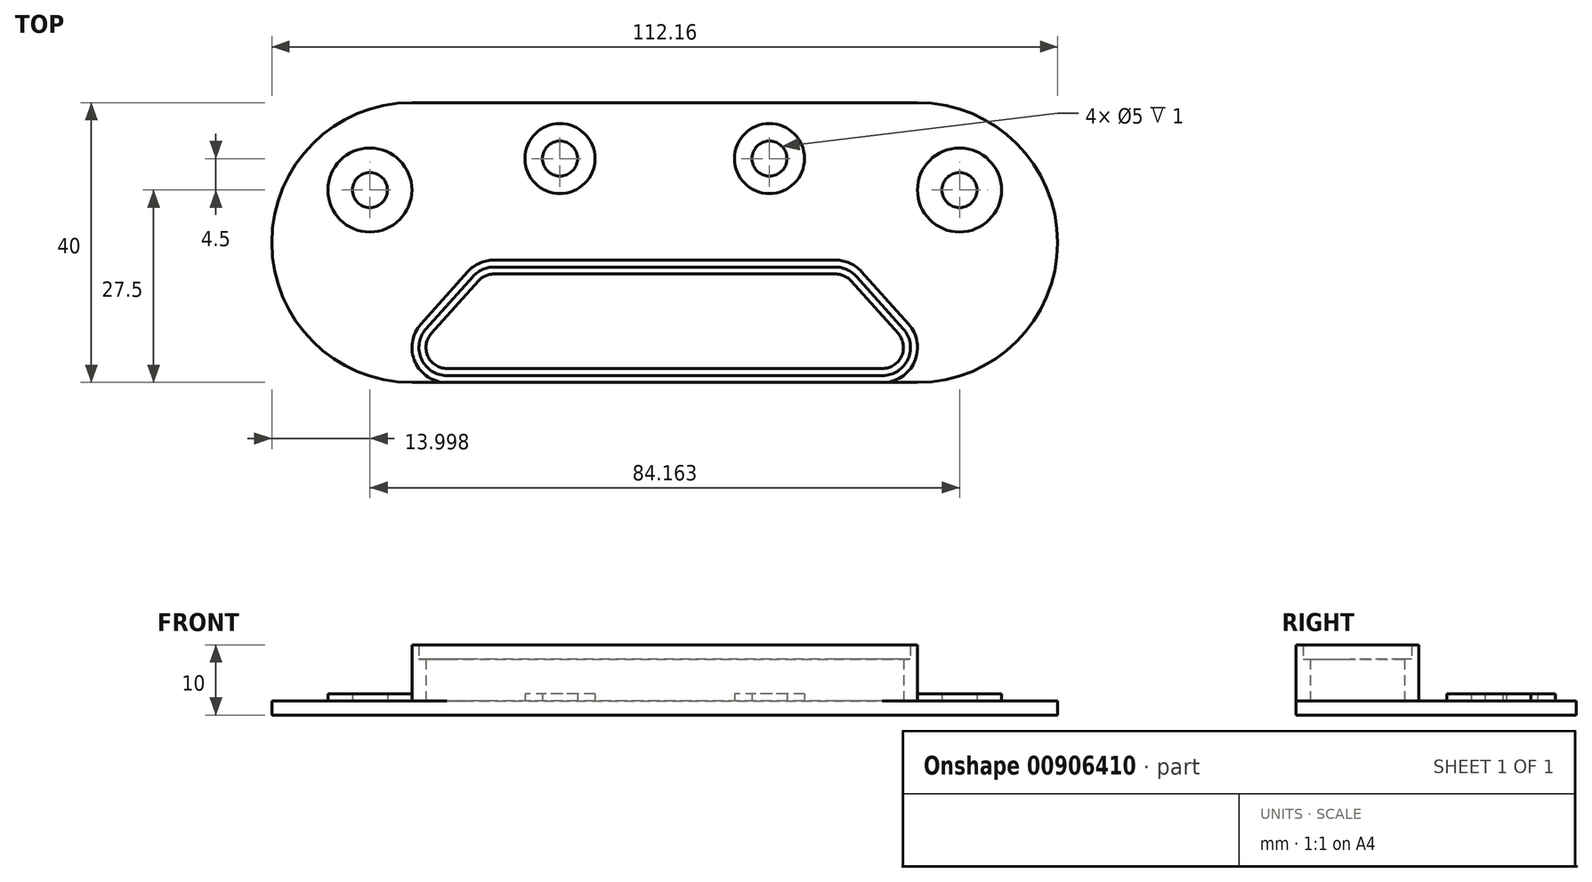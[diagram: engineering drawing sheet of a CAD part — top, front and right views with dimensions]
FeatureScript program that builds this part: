
annotation { "Feature Type Name" : "Feature", "Feature Type Description" : "" }
export const myFeature = defineFeature(function(context is Context, id is Id, definition is map)
    precondition{}
    {
        {
            var Q0;
            Q0=qCreatedBy(makeId("Top.planeOp"),FACE);
            var sketch = newSketch(context, id + "F0", { "sketchPlane" : qUnion([Q0])});
            skLineSegment(sketch, "E0.bottom", {"start": v(36.08, -20) * mm, "end": v(-36.08, -20) * mm});
            skLineSegment(sketch, "E0.top", {"start": v(36.08, 20) * mm, "end": v(-36.08, 20) * mm});
            skLineSegment(sketch, "E0.left", {"start": v(56.08, 0) * mm, "end": v(56.08, 0) * mm});
            skLineSegment(sketch, "E0.right", {"start": v(-56.08, 0) * mm, "end": v(-56.08, 0) * mm});
            skPoint(sketch, "E0.middle", {"position": v(0, 0) * mm});
            skPoint(sketch, "E1.visualSharp", {"position": v(-56.08, -20) * mm});
            skArc(sketch, "E1.filletArc", {"start": v(-56.08, 0) * mm, "mid": v(-50.22, -14.14) * mm, "end": v(-36.08, -20) * mm});
            skPoint(sketch, "E2.visualSharp", {"position": v(-56.08, 20) * mm});
            skArc(sketch, "E2.filletArc", {"start": v(-36.08, 20) * mm, "mid": v(-50.22, 14.14) * mm, "end": v(-56.08, 0) * mm});
            skPoint(sketch, "E3.visualSharp", {"position": v(56.08, 20) * mm});
            skArc(sketch, "E3.filletArc", {"start": v(56.08, 0) * mm, "mid": v(50.22, 14.14) * mm, "end": v(36.08, 20) * mm});
            skPoint(sketch, "E4.visualSharp", {"position": v(56.08, -20) * mm});
            skArc(sketch, "E4.filletArc", {"start": v(36.08, -20) * mm, "mid": v(50.22, -14.14) * mm, "end": v(56.08, 0) * mm});
            skSolve(sketch);
        }
        {
            var Q0;
            Q0=qSketchRegion(id+"F0",true);
            extrude(context, id + "F1", {"entities" : qUnion([Q0]), "depth" : 2 * mm, "offsetDistance" : 25 * mm});
        }
        {
            var Q0;
            Q0=makeQuery(id+"F1.opExtrude","CAP_FACE",FACE,{"disambiguationData":[OSD([sQuery(id+"F0.wireOp",EDGE,"E0.bottom"),sQuery(id+"F0.wireOp",EDGE,"E0.top"),sQuery(id+"F0.wireOp",EDGE,"E1.filletArc"),sQuery(id+"F0.wireOp",EDGE,"E2.filletArc"),sQuery(id+"F0.wireOp",EDGE,"E3.filletArc"),sQuery(id+"F0.wireOp",EDGE,"E4.filletArc")])],"isStart":false});
            var sketch = newSketch(context, id + "F2", { "sketchPlane" : qUnion([Q0])});
            skLineSegment(sketch, "E5", {"start": v(-76.8, 0) * mm, "end": v(76.55, 0) * mm, "construction": true});
            skLineSegment(sketch, "E6", {"start": v(0, -28.1) * mm, "end": v(0, 41.06) * mm, "construction": true});
            skPoint(sketch, "E6.endSnap0", {"position": v(0, 20) * mm});
            skCircle(sketch, "E7", {"center": v(-42.08, 7.5) * mm, "radius": 6 * mm});
            skCircle(sketch, "E8", {"center": v(-42.08, 7.5) * mm, "radius": 2.5 * mm});
            skCircle(sketch, "E9", {"center": v(-14.95, 12) * mm, "radius": 5 * mm});
            skCircle(sketch, "E10", {"center": v(-14.95, 12) * mm, "radius": 2.5 * mm});
            skCircle(sketch, "E11.MirrorC", {"center": v(42.08, 7.5) * mm, "radius": 2.5 * mm});
            skCircle(sketch, "E12.MirrorC", {"center": v(42.08, 7.5) * mm, "radius": 6 * mm});
            skCircle(sketch, "E13.MirrorC", {"center": v(14.95, 12) * mm, "radius": 5 * mm});
            skCircle(sketch, "E14.MirrorC", {"center": v(14.95, 12) * mm, "radius": 2.5 * mm});
            skSolve(sketch);
        }
        {
            var Q0;
            Q0=qSketchRegion(id+"F2",true);
            extrude(context, id + "F3", {"entities" : qUnion([Q0]), "operationType" : NewBodyOperationType.ADD, "depth" : 1 * mm, "offsetDistance" : 25 * mm});
        }
        {
            var Q0;
            {var subQ0=sQuery(id+"F0.wireOp",EDGE,"E2.filletArc");var subQ1=sQuery(id+"F0.wireOp",EDGE,"E1.filletArc");var subQ2=sQuery(id+"F0.wireOp",EDGE,"E0.top");var subQ3=sQuery(id+"F0.wireOp",EDGE,"E4.filletArc");var subQ4=sQuery(id+"F0.wireOp",EDGE,"E3.filletArc");var subQ5=sQuery(id+"F0.wireOp",EDGE,"E0.bottom");Q0=makeQuery(id+"F3.boolean.opBoolean","SPLIT",FACE,{"disambiguationData":[TD([makeQuery(id+"F1.opExtrude","SWEPT_FACE",FACE,{"disambiguationData":[OSD([subQ5])]})])],"derivedFrom":makeQuery(id+"F1.opExtrude","CAP_FACE",FACE,{"disambiguationData":[OSD([subQ5,subQ2,subQ1,subQ0,subQ4,subQ3])],"isStart":false})});}
            var sketch = newSketch(context, id + "F4", { "sketchPlane" : qUnion([Q0])});
            skLineSegment(sketch, "E15", {"start": v(0, 31.88) * mm, "end": v(0, -36.97) * mm, "construction": true});
            skLineSegment(sketch, "E16", {"start": v(0, -20) * mm, "end": v(-31.08, -20) * mm});
            skLineSegment(sketch, "E17", {"start": v(-34.8, -11.67) * mm, "end": v(-28.1, -4.17) * mm});
            skLineSegment(sketch, "E18", {"start": v(-24.38, -2.5) * mm, "end": v(0, -2.5) * mm});
            skPoint(sketch, "E19.visualSharp", {"position": v(-42.26, -20) * mm});
            skArc(sketch, "E19.filletArc", {"start": v(-34.8, -11.67) * mm, "mid": v(-35.65, -17.04) * mm, "end": v(-31.08, -20) * mm});
            skPoint(sketch, "E20.visualSharp", {"position": v(-26.61, -2.5) * mm});
            skArc(sketch, "E20.filletArc", {"start": v(-24.38, -2.5) * mm, "mid": v(-26.42, -2.94) * mm, "end": v(-28.1, -4.17) * mm});
            skLineSegment(sketch, "E21.0", {"start": v(0, -19) * mm, "end": v(-31.08, -19) * mm});
            skLineSegment(sketch, "E21.1", {"start": v(-24.38, -3.5) * mm, "end": v(0, -3.5) * mm});
            skArc(sketch, "E21.2", {"start": v(-24.38, -3.5) * mm, "mid": v(-26, -3.85) * mm, "end": v(-27.36, -4.83) * mm});
            skLineSegment(sketch, "E21.3", {"start": v(-34.06, -12.33) * mm, "end": v(-27.36, -4.83) * mm});
            skArc(sketch, "E21.4", {"start": v(-34.06, -12.33) * mm, "mid": v(-34.73, -16.63) * mm, "end": v(-31.08, -19) * mm});
            skPoint(sketch, "E22.MirrorP", {"position": v(26.61, -2.5) * mm});
            skLineSegment(sketch, "E23.MirrorCS", {"start": v(0, -19) * mm, "end": v(31.08, -19) * mm});
            skArc(sketch, "E24.MirrorCS", {"start": v(24.38, -2.5) * mm, "mid": v(26.42, -2.94) * mm, "end": v(28.1, -4.17) * mm});
            skArc(sketch, "E25.MirrorCS", {"start": v(34.06, -12.33) * mm, "mid": v(34.73, -16.63) * mm, "end": v(31.08, -19) * mm});
            skLineSegment(sketch, "E26.MirrorCS", {"start": v(34.06, -12.33) * mm, "end": v(27.36, -4.83) * mm});
            skLineSegment(sketch, "E27.MirrorCS", {"start": v(24.38, -3.5) * mm, "end": v(0, -3.5) * mm});
            skLineSegment(sketch, "E28.MirrorCS", {"start": v(24.38, -2.5) * mm, "end": v(0, -2.5) * mm});
            skArc(sketch, "E29.MirrorCS", {"start": v(24.38, -3.5) * mm, "mid": v(26, -3.85) * mm, "end": v(27.36, -4.83) * mm});
            skLineSegment(sketch, "E30.MirrorCS", {"start": v(0, -20) * mm, "end": v(31.08, -20) * mm});
            skLineSegment(sketch, "E31.MirrorCS", {"start": v(34.8, -11.67) * mm, "end": v(28.1, -4.17) * mm});
            skArc(sketch, "E32.MirrorCS", {"start": v(34.8, -11.67) * mm, "mid": v(35.65, -17.04) * mm, "end": v(31.08, -20) * mm});
            skSolve(sketch);
        }
        {
            var Q0;
            Q0=qSketchRegion(id+"F4",true);
            extrude(context, id + "F5", {"entities" : qUnion([Q0]), "operationType" : NewBodyOperationType.ADD, "depth" : 8 * mm, "offsetDistance" : 25 * mm});
        }
        {
            var Q0;
            {var subQ3=sQuery(id+"F0.wireOp",EDGE,"E2.filletArc");var subQ4=sQuery(id+"F0.wireOp",EDGE,"E1.filletArc");var subQ6=sQuery(id+"F0.wireOp",EDGE,"E0.bottom");var subQ7=makeQuery(id+"F1.opExtrude","SWEPT_FACE",FACE,{"disambiguationData":[OSD([subQ6])]});var subQ9=sQuery(id+"F0.wireOp",EDGE,"E4.filletArc");var subQ10=sQuery(id+"F0.wireOp",EDGE,"E3.filletArc");var subQ12=sQuery(id+"F0.wireOp",EDGE,"E0.top");Q0=makeQuery(id+"F5.boolean.opBoolean","SPLIT",FACE,{"disambiguationData":[TD([subQ7])],"derivedFrom":makeQuery(id+"F3.boolean.opBoolean","SPLIT",FACE,{"disambiguationData":[TD([subQ7])],"derivedFrom":makeQuery(id+"F1.opExtrude","CAP_FACE",FACE,{"disambiguationData":[OSD([subQ6,subQ12,subQ4,subQ3,subQ10,subQ9])],"isStart":false})})});}
            var sketch = newSketch(context, id + "F6", { "sketchPlane" : qUnion([Q0])});
            skArc(sketch, "E33.0.0", {"start": v(-24.38, -3.5) * mm, "mid": v(-26, -3.85) * mm, "end": v(-27.36, -4.83) * mm});
            skLineSegment(sketch, "E33.0.1", {"start": v(-27.36, -4.83) * mm, "end": v(-34.06, -12.33) * mm});
            skArc(sketch, "E33.0.2", {"start": v(-34.06, -12.33) * mm, "mid": v(-34.73, -16.63) * mm, "end": v(-31.08, -19) * mm});
            skLineSegment(sketch, "E33.0.3", {"start": v(-31.08, -19) * mm, "end": v(31.08, -19) * mm});
            skArc(sketch, "E33.0.4", {"start": v(31.08, -19) * mm, "mid": v(34.73, -16.63) * mm, "end": v(34.06, -12.33) * mm});
            skLineSegment(sketch, "E33.0.5", {"start": v(34.06, -12.33) * mm, "end": v(27.36, -4.83) * mm});
            skArc(sketch, "E33.0.6", {"start": v(27.36, -4.83) * mm, "mid": v(26, -3.85) * mm, "end": v(24.38, -3.5) * mm});
            skLineSegment(sketch, "E33.0.7", {"start": v(24.38, -3.5) * mm, "end": v(-24.38, -3.5) * mm});
            skArc(sketch, "E34.0", {"start": v(26.61, -5.5) * mm, "mid": v(25.6, -4.76) * mm, "end": v(24.38, -4.5) * mm});
            skLineSegment(sketch, "E34.1", {"start": v(33.32, -13) * mm, "end": v(26.61, -5.5) * mm});
            skLineSegment(sketch, "E34.2", {"start": v(24.38, -4.5) * mm, "end": v(-24.38, -4.5) * mm});
            skArc(sketch, "E34.3", {"start": v(31.08, -18) * mm, "mid": v(33.82, -16.22) * mm, "end": v(33.32, -13) * mm});
            skArc(sketch, "E34.4", {"start": v(-24.38, -4.5) * mm, "mid": v(-25.6, -4.76) * mm, "end": v(-26.61, -5.5) * mm});
            skLineSegment(sketch, "E34.5", {"start": v(-26.61, -5.5) * mm, "end": v(-33.32, -13) * mm});
            skArc(sketch, "E34.6", {"start": v(-33.32, -13) * mm, "mid": v(-33.82, -16.22) * mm, "end": v(-31.08, -18) * mm});
            skLineSegment(sketch, "E34.7", {"start": v(-31.08, -18) * mm, "end": v(31.08, -18) * mm});
            skSolve(sketch);
        }
        {
            var Q0;
            Q0=qSketchRegion(id+"F6",true);
            extrude(context, id + "F7", {"entities" : qUnion([Q0]), "operationType" : NewBodyOperationType.ADD, "depth" : 6 * mm, "offsetDistance" : 25 * mm});
        }
    });
